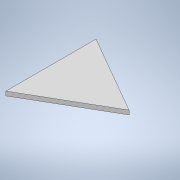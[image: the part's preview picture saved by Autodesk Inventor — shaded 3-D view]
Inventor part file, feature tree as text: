
AUTODESK INVENTOR PART (.ipt)
format: ipt  version: 2022.3 (Build 263350000, 350)  size: 93,184 bytes
history: native  units: in
note: dims shown in document units (in); Inventor stores cm internally (conversion verified against a paired STEP export)
features: extrude x1, sketch x1
ambient origin geometry x8: Origin, YZ Plane, XZ Plane, XY Plane, X Axis, Y Axis, Z Axis, Center Point
bodies: Solid1 (feature_tree)
feature tree (2):
  extrude  "Extrusion1"  [1 undecoded]
  sketch  "Sketch1"  dims[d1=0.1575in d2=0.0in]
note: 1 required parameter value undecoded (feature->parameter linkage not recoverable at this tier; creation-order binding heuristic only, values carry confidence <= 0.55)
